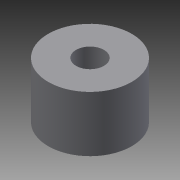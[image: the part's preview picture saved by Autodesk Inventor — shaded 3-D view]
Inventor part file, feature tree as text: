
AUTODESK INVENTOR PART (.ipt)
format: ipt  version: 2013 SP2 (Build 170200200, 200)  size: 73,216 bytes
history: native  units: mm
features: extrude x1, sketch x1
ambient origin geometry x8: Origin, YZ Plane, XZ Plane, XY Plane, X Axis, Y Axis, Z Axis, Center Point
bodies: Solid1 (feature_tree)
feature tree (2):
  extrude  "Extrusion1"  Depth=10.0mm TaperAngle=0.0deg
  sketch  "Sketch1"  dims[d0=15.0mm d1=10.0mm d2=0.0mm d3=5.0mm]
